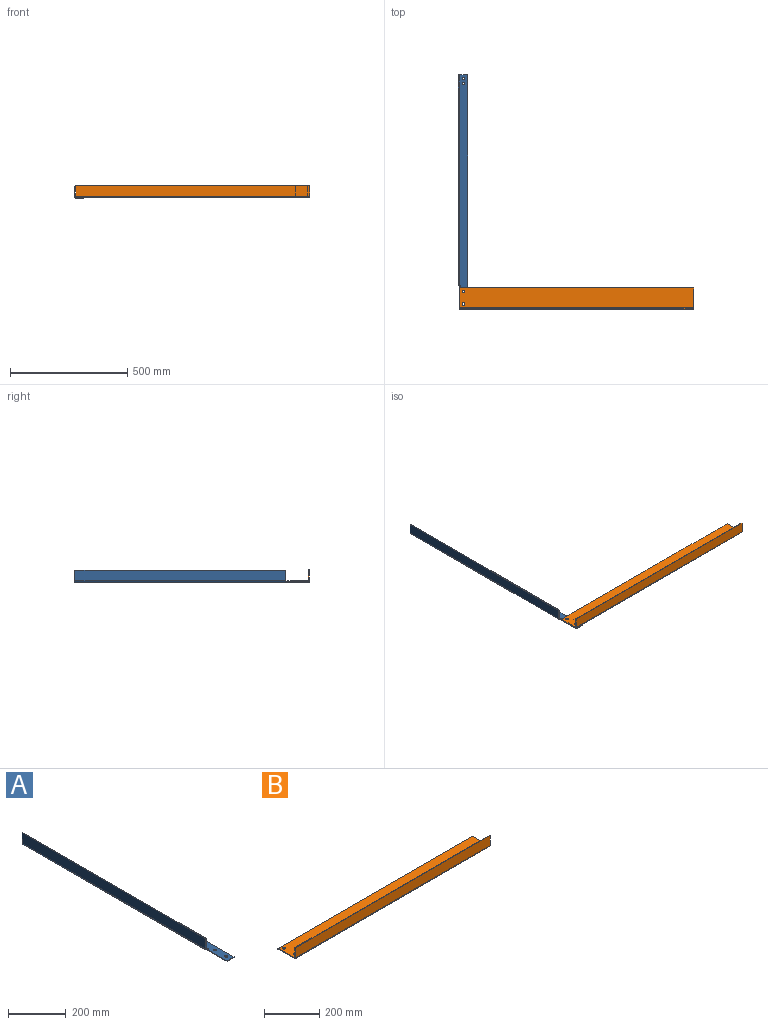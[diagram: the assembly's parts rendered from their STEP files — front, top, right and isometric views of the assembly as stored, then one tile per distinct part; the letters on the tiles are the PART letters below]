
ASSEMBLY  parts=2 mates=1
PART A: 22 faces, bbox 40x1000x50 mm
  f0: plane 34x3mm, normal (0,-1,0), area 102mm2, adj f1,f7,f8,f9
  f1: plane 1000x3mm, normal (1,0,0), area 3000mm2, adj f0,f2,f8,f9
  f2: plane 34x3mm, normal (0,1,0), area 102mm2, adj f1,f8,f9,f19
  f3: cylinder r=5.5mm len=11mm, axis (0,0,1), area 103.7mm2, adj f8,f9
  f4: cylinder r=5.5mm len=11mm, axis (0,0,1), area 103.7mm2, adj f8,f9
  f5: cylinder r=5.5mm len=11mm, axis (0,0,1), area 103.7mm2, adj f8,f9
  f6: cylinder r=5.5mm len=11mm, axis (0,0,1), area 103.7mm2, adj f8,f9
  f7: plane 96.81x3mm, normal (-1,0,0), area 290.4mm2, adj f0,f8,f9,f11
  f8: plane 1000x34mm, normal (0,0,1), area 33606.3mm2, adj f0,f1,f2,f3,f4,f5,f6,f7
  f9: plane 1000x34mm, normal (0,0,-1), area 33606.3mm2, adj f0,f1,f2,f3,f4,f5,f6,f7
  f10: cylinder r=1.59mm len=3.19mm, axis (0,0,-1), area 15mm2, adj f8,f9,f11,f12
  f11: plane 3x3mm, normal (0,1,0), area 9mm2, adj f7,f8,f9,f10
  f12: plane 3x3mm, normal (0,-1,0), area 9mm2, adj f8,f9,f10,f18
  f13: plane 44x3mm, normal (0,1,0), area 132mm2, adj f14,f16,f17,f19
  f14: plane 900x3mm, normal (0,0,1), area 2700mm2, adj f13,f15,f16,f17
  f15: plane 44x3mm, normal (0,-1,0), area 132mm2, adj f14,f16,f17,f18
  f16: plane 900x44mm, normal (1,0,0), area 39600mm2, adj f13,f14,f15,f21
  f17: plane 900x44mm, normal (-1,0,0), area 39600mm2, adj f13,f14,f15,f20
  f18: plane 6x6mm, normal (0,-1,0), area 21.2mm2, adj f12,f15,f20,f21
  f19: plane 6x6mm, normal (0,1,0), area 21.2mm2, adj f2,f13,f20,f21
  f20: cylinder r=6mm len=900mm, axis (0,-1,0), area 8482.3mm2, adj f9,f17,f18,f19
  f21: cylinder r=3mm len=900mm, axis (0,-1,0), area 4241.2mm2, adj f8,f16,f18,f19
PART B: 18 faces, bbox 1000x90x50 mm
  f0: plane 50x44mm, normal (0,1,0), area 2200mm2, adj f1,f10,f12,f17
  f1: plane 44x10mm, normal (0,1,0), area 440mm2, adj f0,f10,f11,f17
  f2: plane 84x3mm, normal (-1,0,0), area 252mm2, adj f6,f7,f8,f15
  f3: plane 84x3mm, normal (1,0,0), area 252mm2, adj f6,f7,f8,f14
  f4: cylinder r=5.5mm len=11mm, axis (0,0,1), area 103.7mm2, adj f7,f8
  f5: cylinder r=5.5mm len=11mm, axis (0,0,1), area 103.7mm2, adj f7,f8
  f6: plane 1000x3mm, normal (0,1,0), area 3000mm2, adj f2,f3,f7,f8
  f7: plane 1000x84mm, normal (0,0,1), area 83809.9mm2, adj f2,f3,f4,f5,f6,f17
  f8: plane 1000x84mm, normal (0,0,-1), area 83809.9mm2, adj f2,f3,f4,f5,f6,f16
  f9: plane 44x3mm, normal (-1,0,0), area 132mm2, adj f10,f12,f13,f15
  f10: plane 1000x3mm, normal (0,0,1), area 3000mm2, adj f0,f1,f9,f11,f12,f13
  f11: plane 44x3mm, normal (1,0,0), area 132mm2, adj f1,f10,f13,f14
  f12: plane 940x44mm, normal (0,1,0), area 41360mm2, adj f0,f9,f10,f17
  f13: plane 1000x44mm, normal (0,-1,0), area 44000mm2, adj f9,f10,f11,f16
  f14: plane 6x6mm, normal (1,0,0), area 21.2mm2, adj f3,f11,f16,f17
  f15: plane 6x6mm, normal (-1,0,0), area 21.2mm2, adj f2,f9,f16,f17
  f16: cylinder r=6mm len=1000mm, axis (1,0,0), area 9424.8mm2, adj f8,f13,f14,f15
  f17: cylinder r=3mm len=1000mm, axis (1,0,0), area 4712.4mm2, adj f0,f1,f7,f12,f14,f15
PLACE A at identity fixed
PLACE B at identity
MATE fastened A.f6 <-> B.f5  axis (0,0,1) through (23,-925.5,3)mm
